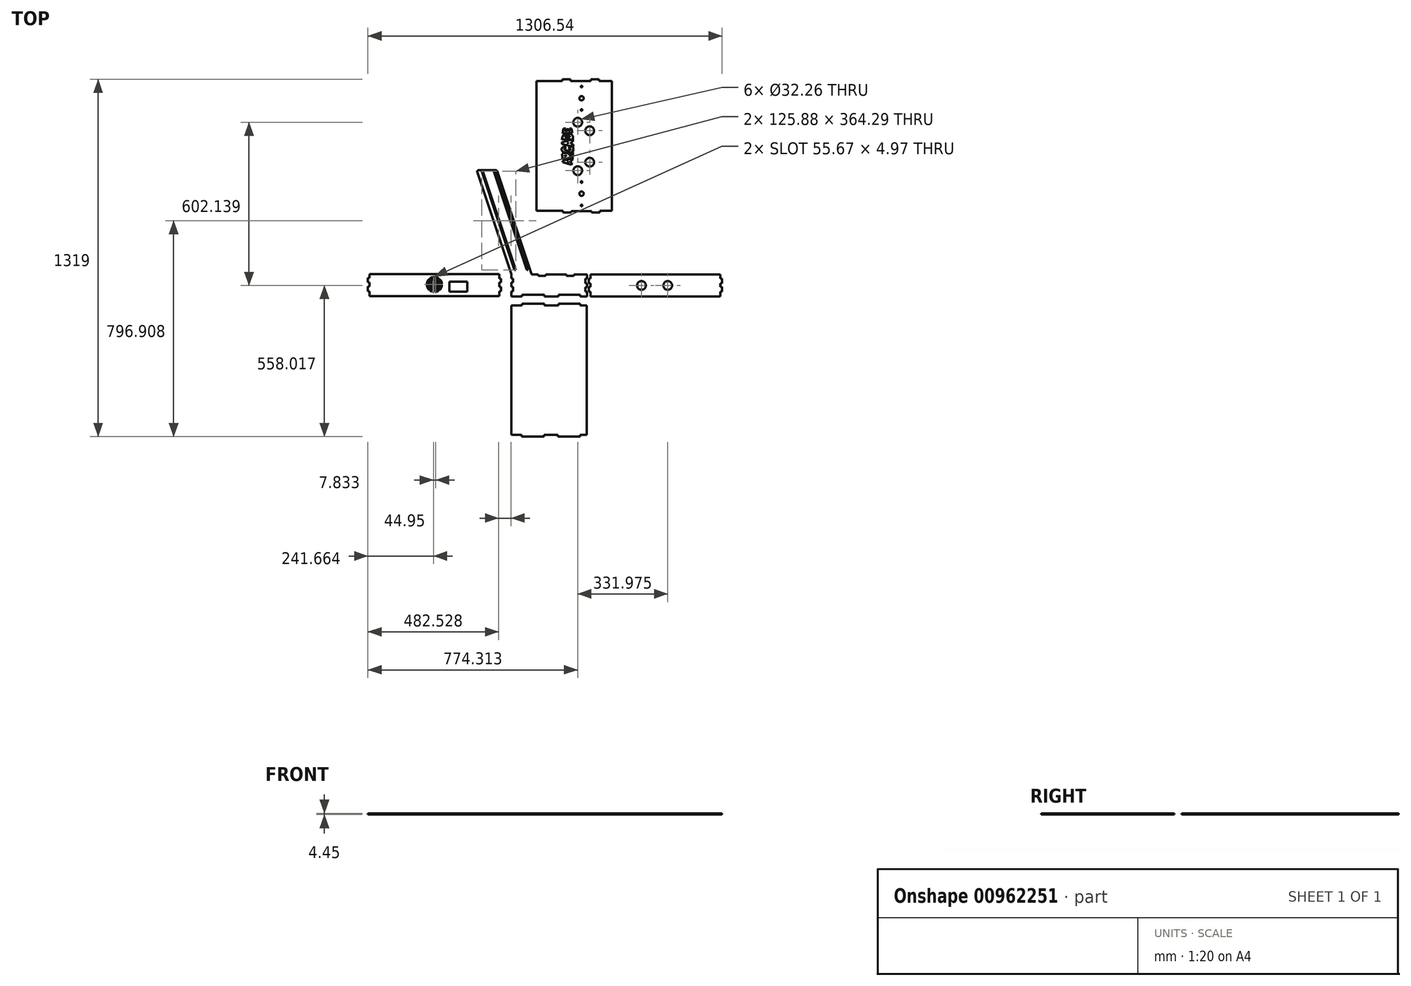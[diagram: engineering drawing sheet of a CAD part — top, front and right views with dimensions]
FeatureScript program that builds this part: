
annotation { "Feature Type Name" : "Feature", "Feature Type Description" : "" }
export const myFeature = defineFeature(function(context is Context, id is Id, definition is map)
    precondition{}
    {
        {
            var Q0;
            Q0=qCreatedBy(makeId("Top.planeOp"),FACE);
            var sketch = newSketch(context, id + "F0", { "sketchPlane" : qUnion([Q0])});
            skLineSegment(sketch, "E0.0", {"start": v(-133.22, 195.57) * mm, "end": v(-13.13, -164.7) * mm});
            skLineSegment(sketch, "E0.2", {"start": v(-206.4, 192.41) * mm, "end": v(-84, -174.81) * mm});
            skLineSegment(sketch, "E1", {"start": v(-84, -174.81) * mm, "end": v(-80.85, -184.23) * mm});
            skLineSegment(sketch, "E2", {"start": v(-13.13, -164.7) * mm, "end": v(-7.25, -182.33) * mm});
            skPoint(sketch, "E3.start.orphan", {"position": v(-23.94, -169.52) * mm});
            skLineSegment(sketch, "E4.bottom", {"start": v(-2.51, -185.75) * mm, "end": v(17.92, -185.75) * mm});
            skLineSegment(sketch, "E4.right", {"start": v(199.34, -185.75) * mm, "end": v(199.34, -201.04) * mm});
            skLineSegment(sketch, "E5", {"start": v(-129.53, 12.4) * mm, "end": v(-125.08, 12.4) * mm});
            skLineSegment(sketch, "E6", {"start": v(-89.03, 12.4) * mm, "end": v(-93.48, 12.4) * mm});
            skLineSegment(sketch, "E7.left", {"start": v(-80.35, -185.75) * mm, "end": v(-80.35, -201.04) * mm});
            skPoint(sketch, "E8.end.orphan", {"position": v(-48.56, -185.75) * mm});
            skLineSegment(sketch, "E9", {"start": v(-188.02, 199) * mm, "end": v(-201.66, 199) * mm});
            skLineSegment(sketch, "E10", {"start": v(-188.02, 199) * mm, "end": v(-137.97, 199) * mm});
            skPoint(sketch, "E11.start.orphan", {"position": v(-188.02, 194.54) * mm});
            skLineSegment(sketch, "E12.bottom", {"start": v(45.83, -190.2) * mm, "end": v(18.43, -190.2) * mm});
            skLineSegment(sketch, "E12.left", {"start": v(45.83, -190.2) * mm, "end": v(45.32, -185.75) * mm});
            skLineSegment(sketch, "E12.right", {"start": v(18.43, -190.2) * mm, "end": v(17.92, -185.75) * mm});
            skPoint(sketch, "E12.middle", {"position": v(31.62, -185.75) * mm});
            skPoint(sketch, "E13.middle", {"position": v(159.6, -185.75) * mm});
            skPoint(sketch, "E12.top.end.orphan", {"position": v(17.41, -181.3) * mm});
            skPoint(sketch, "E14.orphan", {"position": v(44.81, -181.3) * mm});
            skPoint(sketch, "E13.top.end.orphan", {"position": v(142.34, -174.18) * mm});
            skPoint(sketch, "E15.orphan", {"position": v(176.85, -174.18) * mm});
            skLineSegment(sketch, "E16.bottom", {"start": v(149.99, -190.2) * mm, "end": v(122.59, -190.2) * mm});
            skLineSegment(sketch, "E16.left", {"start": v(149.99, -190.2) * mm, "end": v(149.98, -185.75) * mm});
            skLineSegment(sketch, "E16.right", {"start": v(122.59, -190.2) * mm, "end": v(122.58, -185.75) * mm});
            skLineSegment(sketch, "E17.trimOffspring", {"start": v(45.32, -185.75) * mm, "end": v(122.58, -185.75) * mm});
            skLineSegment(sketch, "E18.trimOffspring", {"start": v(149.98, -185.75) * mm, "end": v(199.34, -185.75) * mm});
            skLineSegment(sketch, "E19.bottom", {"start": v(199.34, -218.57) * mm, "end": v(193, -218.57) * mm});
            skLineSegment(sketch, "E19.top", {"start": v(199.34, -201.04) * mm, "end": v(193, -201.04) * mm});
            skLineSegment(sketch, "E19.right", {"start": v(193, -218.57) * mm, "end": v(193, -201.04) * mm});
            skPoint(sketch, "E19.middle", {"position": v(199.34, -209.8) * mm});
            skPoint(sketch, "E19.left.end.orphan", {"position": v(205.67, -201.04) * mm});
            skPoint(sketch, "E20.orphan", {"position": v(205.67, -218.57) * mm});
            skLineSegment(sketch, "E21.trimOffspring", {"start": v(199.34, -218.57) * mm, "end": v(199.34, -232.97) * mm});
            skLineSegment(sketch, "E22.bottom", {"start": v(199.34, -248.5) * mm, "end": v(193, -248.5) * mm});
            skLineSegment(sketch, "E22.top", {"start": v(199.34, -232.97) * mm, "end": v(193, -232.97) * mm});
            skLineSegment(sketch, "E22.right", {"start": v(193, -248.5) * mm, "end": v(193, -232.97) * mm});
            skLineSegment(sketch, "E23.trimOffspring", {"start": v(199.34, -248.5) * mm, "end": v(199.34, -266.77) * mm});
            skLineSegment(sketch, "E24.bottom", {"start": v(109.66, 43.6) * mm, "end": v(140.06, 43.6) * mm});
            skLineSegment(sketch, "E24.left", {"start": v(109.66, 43.6) * mm, "end": v(109.66, 49.94) * mm});
            skLineSegment(sketch, "E24.right", {"start": v(140.06, 43.6) * mm, "end": v(140.06, 48.06) * mm});
            skLineSegment(sketch, "E25.top", {"start": v(214.83, 43.6) * mm, "end": v(245.23, 43.6) * mm});
            skLineSegment(sketch, "E25.left", {"start": v(214.83, 48.06) * mm, "end": v(214.83, 43.6) * mm});
            skLineSegment(sketch, "E25.right", {"start": v(245.23, 49.94) * mm, "end": v(245.23, 43.6) * mm});
            skLineSegment(sketch, "E26", {"start": v(86.13, 49.94) * mm, "end": v(109.66, 49.94) * mm});
            skLineSegment(sketch, "E27", {"start": v(140.06, 48.06) * mm, "end": v(214.83, 48.06) * mm});
            skLineSegment(sketch, "E28", {"start": v(245.23, 49.94) * mm, "end": v(289.7, 49.94) * mm});
            skLineSegment(sketch, "E29", {"start": v(289.7, 49.94) * mm, "end": v(289.7, 528.39) * mm});
            skLineSegment(sketch, "E30", {"start": v(86.13, 528.39) * mm, "end": v(107.66, 528.39) * mm});
            skLineSegment(sketch, "E31.MirrorCS", {"start": v(107.66, 534.72) * mm, "end": v(107.66, 528.39) * mm});
            skLineSegment(sketch, "E32.MirrorCS", {"start": v(138.06, 534.72) * mm, "end": v(138.06, 528.39) * mm});
            skLineSegment(sketch, "E33.MirrorCS", {"start": v(212.83, 528.39) * mm, "end": v(212.83, 534.72) * mm});
            skLineSegment(sketch, "E34.MirrorCS", {"start": v(243.23, 528.39) * mm, "end": v(243.23, 534.72) * mm});
            skLineSegment(sketch, "E35.trimOffspring", {"start": v(138.06, 528.39) * mm, "end": v(212.83, 528.39) * mm});
            skLineSegment(sketch, "E36.trimOffspring", {"start": v(243.23, 528.39) * mm, "end": v(289.7, 528.39) * mm});
            skPoint(sketch, "E37.start.orphan", {"position": v(86.13, 289.16) * mm});
            skCircle(sketch, "E38", {"center": v(178.38, 507.69) * mm, "radius": 3 * mm});
            skCircle(sketch, "E39", {"center": v(178.38, 421.29) * mm, "radius": 3 * mm});
            skCircle(sketch, "E40", {"center": v(164.4, 375.88) * mm, "radius": 16.13 * mm});
            skCircle(sketch, "E41", {"center": v(208.47, 344.63) * mm, "radius": 16.13 * mm});
            skCircle(sketch, "E42.MirrorC", {"center": v(178.38, 155.57) * mm, "radius": 3 * mm});
            skCircle(sketch, "E43.MirrorC", {"center": v(178.38, 69.17) * mm, "radius": 3 * mm});
            skCircle(sketch, "E44.MirrorC", {"center": v(208.47, 228.58) * mm, "radius": 16.13 * mm});
            skCircle(sketch, "E45.MirrorC", {"center": v(164.4, 197.33) * mm, "radius": 16.13 * mm});
            skCircle(sketch, "E46", {"center": v(178.38, 464.49) * mm, "radius": 8.09 * mm});
            skCircle(sketch, "E47.MirrorC", {"center": v(178.38, 112.37) * mm, "radius": 8.09 * mm});
            skLineSegment(sketch, "E48.MirrorCS", {"start": v(120.12, 254.5) * mm, "end": v(118.38, 254.37) * mm});
            skLineSegment(sketch, "E49.MirrorCS", {"start": v(146.92, 313.16) * mm, "end": v(146.92, 304.04) * mm});
            skLineSegment(sketch, "E50.MirrorCS", {"start": v(146.24, 313.22) * mm, "end": v(146.92, 313.16) * mm});
            skLineSegment(sketch, "E51.MirrorCS", {"start": v(117.25, 254.08) * mm, "end": v(116.34, 253.4) * mm});
            skLineSegment(sketch, "E52.MirrorCS", {"start": v(116.34, 253.4) * mm, "end": v(116, 250.63) * mm});
            skLineSegment(sketch, "E53.MirrorCS", {"start": v(129.87, 228.95) * mm, "end": v(129.87, 231.1) * mm});
            skLineSegment(sketch, "E54.MirrorCS", {"start": v(118.38, 254.37) * mm, "end": v(117.25, 254.08) * mm});
            skLineSegment(sketch, "E55.MirrorCS", {"start": v(121.7, 253.4) * mm, "end": v(120.12, 254.5) * mm});
            skLineSegment(sketch, "E56.MirrorCS", {"start": v(142.11, 234.25) * mm, "end": v(144.38, 234.25) * mm});
            skLineSegment(sketch, "E57.MirrorCS", {"start": v(123.2, 262.9) * mm, "end": v(122.67, 262.98) * mm});
            skLineSegment(sketch, "E58.MirrorCS", {"start": v(116, 250.63) * mm, "end": v(121.7, 250.43) * mm});
            skLineSegment(sketch, "E59.MirrorCS", {"start": v(144.64, 304.04) * mm, "end": v(140.36, 303.04) * mm});
            skLineSegment(sketch, "E60.MirrorCS", {"start": v(121.7, 250.43) * mm, "end": v(121.7, 253.4) * mm});
            skLineSegment(sketch, "E61.MirrorCS", {"start": v(130.78, 258.7) * mm, "end": v(128.56, 260.6) * mm});
            skLineSegment(sketch, "E62.MirrorCS", {"start": v(145.83, 241.97) * mm, "end": v(144.38, 234.25) * mm});
            skLineSegment(sketch, "E63.MirrorCS", {"start": v(138.33, 233.06) * mm, "end": v(142.11, 234.25) * mm});
            skLineSegment(sketch, "E64.MirrorCS", {"start": v(145.08, 255.03) * mm, "end": v(146.64, 255.34) * mm});
            skLineSegment(sketch, "E65.MirrorCS", {"start": v(142.65, 241.97) * mm, "end": v(145.83, 241.97) * mm});
            skLineSegment(sketch, "E66.MirrorCS", {"start": v(140.36, 296.24) * mm, "end": v(145.28, 294.98) * mm});
            skLineSegment(sketch, "E67.MirrorCS", {"start": v(146.92, 304.04) * mm, "end": v(144.64, 304.04) * mm});
            skLineSegment(sketch, "E68.MirrorCS", {"start": v(145.9, 250.5) * mm, "end": v(132.72, 250.5) * mm});
            skLineSegment(sketch, "E69.MirrorCS", {"start": v(140.36, 303.04) * mm, "end": v(140.36, 296.24) * mm});
            skLineSegment(sketch, "E70.MirrorCS", {"start": v(125.05, 299.5) * mm, "end": v(130.81, 298.2) * mm});
            skLineSegment(sketch, "E71.MirrorCS", {"start": v(129.87, 231.1) * mm, "end": v(125.64, 230.28) * mm});
            skLineSegment(sketch, "E72.MirrorCS", {"start": v(123, 224.26) * mm, "end": v(134.99, 220.38) * mm});
            skLineSegment(sketch, "E73.MirrorCS", {"start": v(145.28, 294.98) * mm, "end": v(147.53, 294.98) * mm});
            skLineSegment(sketch, "E74.MirrorCS", {"start": v(130.81, 298.2) * mm, "end": v(130.81, 300.81) * mm});
            skLineSegment(sketch, "E75.MirrorCS", {"start": v(145.62, 242.56) * mm, "end": v(145.9, 250.5) * mm});
            skLineSegment(sketch, "E76.MirrorCS", {"start": v(125.64, 230.28) * mm, "end": v(129.87, 228.95) * mm});
            skLineSegment(sketch, "E77.MirrorCS", {"start": v(141.03, 226.32) * mm, "end": v(137.8, 226.9) * mm});
            skLineSegment(sketch, "E78.MirrorCS", {"start": v(137.8, 226.9) * mm, "end": v(138.33, 233.06) * mm});
            skLineSegment(sketch, "E79.MirrorCS", {"start": v(132.72, 250.5) * mm, "end": v(145.08, 255.03) * mm});
            skLineSegment(sketch, "E80.MirrorCS", {"start": v(147.3, 264.53) * mm, "end": v(130.78, 258.7) * mm});
            skLineSegment(sketch, "E81.MirrorCS", {"start": v(146.64, 255.34) * mm, "end": v(147.3, 264.53) * mm});
            skLineSegment(sketch, "E82.MirrorCS", {"start": v(130.81, 300.81) * mm, "end": v(125.05, 299.5) * mm});
            skLineSegment(sketch, "E83.MirrorCS", {"start": v(143.46, 226.32) * mm, "end": v(141.03, 226.32) * mm});
            skLineSegment(sketch, "E84.MirrorCS", {"start": v(142.65, 241.97) * mm, "end": v(128.56, 238.4) * mm});
            skLineSegment(sketch, "E85.MirrorCS", {"start": v(140.12, 218.92) * mm, "end": v(141.84, 218.2) * mm});
            skLineSegment(sketch, "E86.MirrorCS", {"start": v(135.95, 321.28) * mm, "end": v(135.67, 323.92) * mm});
            skArc(sketch, "E87.MirrorCS", {"start": v(135.67, 323.92) * mm, "mid": v(126.36, 327.54) * mm, "end": v(117.25, 323.41) * mm});
            skLineSegment(sketch, "E88.MirrorCS", {"start": v(107.46, 243.91) * mm, "end": v(145.62, 242.56) * mm});
            skLineSegment(sketch, "E89.MirrorCS", {"start": v(141.84, 218.2) * mm, "end": v(143.46, 226.32) * mm});
            skFitSpline(sketch, "E90.MirrorCS", {"points": [v(128.56, 260.6) * mm, v(123.2, 262.9) * mm, v(114.65, 262.9) * mm, v(107.11, 257.92) * mm, v(107.34, 246.66) * mm, v(107.46, 243.91) * mm, v(131.36, 256.58) * mm, v(128.56, 260.6) * mm]});
            skLineSegment(sketch, "E91.MirrorCS", {"start": v(117.25, 321.28) * mm, "end": v(135.95, 321.28) * mm});
            skLineSegment(sketch, "E92.MirrorCS", {"start": v(131.27, 342.19) * mm, "end": v(130.03, 350.78) * mm});
            skArc(sketch, "E93.MirrorCS", {"start": v(146.24, 324.8) * mm, "mid": v(125.43, 335.33) * mm, "end": v(107.15, 320.84) * mm});
            skLineSegment(sketch, "E94.MirrorCS", {"start": v(108.97, 235.06) * mm, "end": v(109.67, 228.58) * mm});
            skLineSegment(sketch, "E95.MirrorCS", {"start": v(117.25, 341.92) * mm, "end": v(119.47, 353.18) * mm});
            skLineSegment(sketch, "E96.MirrorCS", {"start": v(122.84, 350.78) * mm, "end": v(122.84, 341.92) * mm});
            skLineSegment(sketch, "E97.MirrorCS", {"start": v(134.15, 353.36) * mm, "end": v(135.67, 342.82) * mm});
            skLineSegment(sketch, "E98.MirrorCS", {"start": v(109.67, 228.58) * mm, "end": v(123, 224.26) * mm});
            skLineSegment(sketch, "E99.MirrorCS", {"start": v(119.47, 353.18) * mm, "end": v(111.45, 352.62) * mm});
            skLineSegment(sketch, "E100.MirrorCS", {"start": v(135.67, 342.82) * mm, "end": v(131.27, 342.19) * mm});
            skLineSegment(sketch, "E101.MirrorCS", {"start": v(117.25, 323.41) * mm, "end": v(117.25, 321.28) * mm});
            skLineSegment(sketch, "E102.MirrorCS", {"start": v(147.5, 285.67) * mm, "end": v(105.6, 295.49) * mm});
            skLineSegment(sketch, "E103.MirrorCS", {"start": v(141.7, 353.36) * mm, "end": v(134.15, 353.36) * mm});
            skLineSegment(sketch, "E104.MirrorCS", {"start": v(105.6, 295.49) * mm, "end": v(105.6, 302.4) * mm});
            skLineSegment(sketch, "E105.MirrorCS", {"start": v(130.03, 350.78) * mm, "end": v(122.84, 350.78) * mm});
            skLineSegment(sketch, "E106.MirrorCS", {"start": v(128.56, 238.4) * mm, "end": v(108.97, 235.06) * mm});
            skLineSegment(sketch, "E107.MirrorCS", {"start": v(122.84, 341.92) * mm, "end": v(117.25, 341.92) * mm});
            skLineSegment(sketch, "E108.MirrorCS", {"start": v(111.45, 352.62) * mm, "end": v(108.28, 334.85) * mm});
            skLineSegment(sketch, "E109.MirrorCS", {"start": v(134.99, 220.38) * mm, "end": v(140.12, 218.92) * mm});
            skLineSegment(sketch, "E110.MirrorCS", {"start": v(146.92, 313.7) * mm, "end": v(146.24, 324.8) * mm});
            skLineSegment(sketch, "E111.MirrorCS", {"start": v(105.6, 302.4) * mm, "end": v(146.24, 313.22) * mm});
            skLineSegment(sketch, "E112.MirrorCS", {"start": v(106.5, 312.6) * mm, "end": v(146.92, 313.7) * mm});
            skLineSegment(sketch, "E113.MirrorCS", {"start": v(106.5, 312.6) * mm, "end": v(107.15, 320.84) * mm});
            skLineSegment(sketch, "E114.MirrorCS", {"start": v(143.98, 337.2) * mm, "end": v(141.7, 353.36) * mm});
            skLineSegment(sketch, "E115.MirrorCS", {"start": v(108.28, 334.85) * mm, "end": v(143.98, 337.2) * mm});
            skFitSpline(sketch, "E116.MirrorC", {"points": [v(118.4, 278.2) * mm, v(116.6, 278.05) * mm, v(114.9, 277.2) * mm, v(114.56, 275.62) * mm, v(115.92, 274) * mm, v(121.92, 272.13) * mm, v(128.49, 271.77) * mm, v(134.71, 272.58) * mm, v(138, 274.5) * mm, v(138.34, 276.84) * mm, v(135.73, 277.9) * mm, v(132.68, 278.86) * mm, v(132.68, 279.68) * mm, v(132.62, 286.61) * mm, v(132.68, 287.83) * mm, v(142.87, 285.6) * mm, v(143.54, 285.19) * mm, v(147.96, 281.4) * mm, v(148.3, 273.3) * mm, v(145.36, 268.33) * mm, v(137.77, 264.48) * mm, v(126.67, 263.32) * mm, v(115.01, 264.89) * mm, v(108.45, 268.48) * mm, v(105.05, 272.38) * mm, v(104.54, 276.89) * mm, v(106.18, 281.85) * mm, v(112.01, 286) * mm, v(117.28, 287.53) * mm, v(118.4, 287.58) * mm, v(118.64, 285.19) * mm, v(118.4, 278.2) * mm]});
            skLineSegment(sketch, "E117", {"start": v(147.53, 294.98) * mm, "end": v(147.5, 285.67) * mm});
            skLineSegment(sketch, "E118.bottom", {"start": v(211.85, -185.75) * mm, "end": v(690.3, -185.75) * mm});
            skLineSegment(sketch, "E118.top", {"start": v(211.85, -266.77) * mm, "end": v(690.3, -266.77) * mm});
            skLineSegment(sketch, "E118.left", {"start": v(211.85, -185.75) * mm, "end": v(211.85, -201.04) * mm});
            skLineSegment(sketch, "E118.right", {"start": v(690.3, -185.75) * mm, "end": v(690.3, -201.04) * mm});
            skLineSegment(sketch, "E119.bottom", {"start": v(211.85, -201.04) * mm, "end": v(205.52, -201.04) * mm});
            skLineSegment(sketch, "E119.top", {"start": v(211.85, -218.57) * mm, "end": v(205.52, -218.57) * mm});
            skLineSegment(sketch, "E119.right", {"start": v(205.52, -201.04) * mm, "end": v(205.52, -218.57) * mm});
            skLineSegment(sketch, "E120.top", {"start": v(211.85, -248.5) * mm, "end": v(205.52, -248.5) * mm});
            skLineSegment(sketch, "E120.right", {"start": v(205.52, -230.97) * mm, "end": v(205.52, -248.5) * mm});
            skCircle(sketch, "E121", {"center": v(399.43, -226.26) * mm, "radius": 16.13 * mm});
            skPoint(sketch, "E121.centerSnap0", {"position": v(211.85, -226.26) * mm});
            skCircle(sketch, "E122.MirrorC", {"center": v(496.38, -226.26) * mm, "radius": 16.13 * mm});
            skPoint(sketch, "E123.start.orphan", {"position": v(451.07, -185.75) * mm});
            skLineSegment(sketch, "E124.MirrorCS", {"start": v(690.3, -230.97) * mm, "end": v(696.63, -230.97) * mm});
            skLineSegment(sketch, "E125.MirrorCS", {"start": v(690.3, -248.5) * mm, "end": v(696.63, -248.5) * mm});
            skLineSegment(sketch, "E126.MirrorCS", {"start": v(690.3, -218.57) * mm, "end": v(696.63, -218.57) * mm});
            skLineSegment(sketch, "E127.MirrorCS", {"start": v(690.3, -201.04) * mm, "end": v(696.63, -201.04) * mm});
            skLineSegment(sketch, "E128.trimOffspring", {"start": v(211.85, -218.57) * mm, "end": v(211.85, -226.26) * mm});
            skLineSegment(sketch, "E129.trimOffspring", {"start": v(211.85, -248.5) * mm, "end": v(211.85, -266.77) * mm});
            skLineSegment(sketch, "E130.trimOffspring", {"start": v(690.3, -248.5) * mm, "end": v(690.3, -266.77) * mm});
            skLineSegment(sketch, "E131.trimOffspring", {"start": v(690.3, -218.57) * mm, "end": v(690.3, -230.97) * mm});
            skLineSegment(sketch, "E132.trimOffspring", {"start": v(-80.35, -248.5) * mm, "end": v(-80.35, -266.77) * mm});
            skPoint(sketch, "E133.start.orphan", {"position": v(59.5, -266.77) * mm});
            skPoint(sketch, "E134.middle", {"position": v(-577.81, -208.7) * mm});
            skPoint(sketch, "E134.left.end.orphan", {"position": v(-573.36, -199.94) * mm});
            skPoint(sketch, "E135.orphan", {"position": v(-573.36, -217.46) * mm});
            skLineSegment(sketch, "E136.bottom", {"start": v(-603.58, -184.65) * mm, "end": v(-125.08, -184.65) * mm});
            skLineSegment(sketch, "E136.top", {"start": v(-603.58, -265.67) * mm, "end": v(-125.08, -265.67) * mm});
            skLineSegment(sketch, "E136.left", {"start": v(-603.58, -184.65) * mm, "end": v(-603.58, -197.94) * mm});
            skLineSegment(sketch, "E136.right", {"start": v(-125.08, -184.65) * mm, "end": v(-125.08, -200.94) * mm});
            skLineSegment(sketch, "E137.bottom", {"start": v(-603.58, -197.94) * mm, "end": v(-609.9, -197.94) * mm});
            skLineSegment(sketch, "E137.top", {"start": v(-603.58, -215.46) * mm, "end": v(-609.9, -215.46) * mm});
            skLineSegment(sketch, "E137.right", {"start": v(-609.9, -197.94) * mm, "end": v(-609.9, -215.46) * mm});
            skLineSegment(sketch, "E138.bottom", {"start": v(-603.58, -229.86) * mm, "end": v(-609.9, -229.86) * mm});
            skLineSegment(sketch, "E138.top", {"start": v(-603.58, -247.39) * mm, "end": v(-609.9, -247.39) * mm});
            skLineSegment(sketch, "E138.right", {"start": v(-609.9, -229.86) * mm, "end": v(-609.9, -247.39) * mm});
            skPoint(sketch, "E139.centerSnap0", {"position": v(-563.42, -225.16) * mm});
            skPoint(sketch, "E140.start.orphan", {"position": v(-324.17, -184.65) * mm});
            skLineSegment(sketch, "E141.MirrorCS", {"start": v(-125.08, -247.39) * mm, "end": v(-118.75, -247.39) * mm});
            skLineSegment(sketch, "E142.MirrorCS", {"start": v(-125.08, -215.46) * mm, "end": v(-118.75, -215.46) * mm});
            skLineSegment(sketch, "E143.MirrorCS", {"start": v(-125.08, -200.94) * mm, "end": v(-118.75, -200.94) * mm});
            skLineSegment(sketch, "E144.trimOffspring", {"start": v(-603.58, -215.46) * mm, "end": v(-603.58, -229.86) * mm});
            skLineSegment(sketch, "E145.trimOffspring", {"start": v(-603.58, -247.39) * mm, "end": v(-603.58, -265.67) * mm});
            skLineSegment(sketch, "E146.trimOffspring", {"start": v(-125.08, -247.39) * mm, "end": v(-125.08, -265.67) * mm});
            skLineSegment(sketch, "E147.trimOffspring", {"start": v(-125.08, -215.46) * mm, "end": v(-125.08, -229.86) * mm});
            skPoint(sketch, "E148.middle", {"position": v(0, -266.77) * mm});
            skPoint(sketch, "E149.orphan", {"position": v(-41.14, -273.1) * mm});
            skPoint(sketch, "E150.orphan", {"position": v(41.14, -273.1) * mm});
            skLineSegment(sketch, "E151.bottom", {"start": v(-80.35, -299.5) * mm, "end": v(-41.14, -299.5) * mm});
            skLineSegment(sketch, "E151.left", {"start": v(-80.35, -299.5) * mm, "end": v(-80.35, -773.5) * mm});
            skLineSegment(sketch, "E152.top", {"start": v(93.97, -293.17) * mm, "end": v(172.76, -293.17) * mm});
            skLineSegment(sketch, "E152.left", {"start": v(93.97, -299.5) * mm, "end": v(93.97, -293.17) * mm});
            skLineSegment(sketch, "E153.trimOffspring", {"start": v(41.14, -299.5) * mm, "end": v(93.97, -299.5) * mm});
            skLineSegment(sketch, "E154.trimOffspring", {"start": v(175.66, -299.5) * mm, "end": v(197.46, -299.5) * mm});
            skLineSegment(sketch, "E155.MirrorCS", {"start": v(-42.14, -773.5) * mm, "end": v(-42.14, -777.95) * mm});
            skLineSegment(sketch, "E156.MirrorCS", {"start": v(40.14, -777.95) * mm, "end": v(40.14, -784.28) * mm});
            skLineSegment(sketch, "E157.MirrorCS", {"start": v(91.37, -777.95) * mm, "end": v(91.37, -784.28) * mm});
            skLineSegment(sketch, "E158.MirrorCS", {"start": v(173.66, -777.95) * mm, "end": v(173.66, -784.28) * mm});
            skLineSegment(sketch, "E159.trimOffspring", {"start": v(40.14, -777.95) * mm, "end": v(91.37, -777.95) * mm});
            skPoint(sketch, "E160.start.orphan", {"position": v(-80.35, -536.5) * mm});
            skLineSegment(sketch, "E161.trimOffspring", {"start": v(173.66, -777.95) * mm, "end": v(197.46, -777.95) * mm});
            skLineSegment(sketch, "E162", {"start": v(696.63, -201.04) * mm, "end": v(696.63, -218.57) * mm});
            skLineSegment(sketch, "E163", {"start": v(696.63, -230.97) * mm, "end": v(696.63, -248.5) * mm});
            skLineSegment(sketch, "E164", {"start": v(-118.75, -215.46) * mm, "end": v(-118.75, -200.94) * mm});
            skLineSegment(sketch, "E165", {"start": v(-118.75, -230.86) * mm, "end": v(-118.75, -247.39) * mm});
            skLineSegment(sketch, "E166", {"start": v(107.66, 534.72) * mm, "end": v(138.06, 534.72) * mm});
            skLineSegment(sketch, "E167", {"start": v(212.83, 534.72) * mm, "end": v(243.23, 534.72) * mm});
            skLineSegment(sketch, "E168", {"start": v(173.66, -784.28) * mm, "end": v(91.37, -784.28) * mm});
            skLineSegment(sketch, "E169", {"start": v(40.14, -784.28) * mm, "end": v(-42.14, -784.28) * mm});
            skLineSegment(sketch, "E170", {"start": v(-42.14, -784.28) * mm, "end": v(-42.14, -777.95) * mm});
            skLineSegment(sketch, "E171", {"start": v(-80.35, -773.5) * mm, "end": v(-80.35, -777.95) * mm});
            skLineSegment(sketch, "E172", {"start": v(-80.35, -777.95) * mm, "end": v(-42.14, -777.95) * mm});
            skLineSegment(sketch, "E173.bottom", {"start": v(86.13, 49.94) * mm, "end": v(11.9, 49.94) * mm});
            skLineSegment(sketch, "E173.top", {"start": v(86.13, 528.39) * mm, "end": v(11.9, 528.39) * mm});
            skLineSegment(sketch, "E173.right", {"start": v(11.9, 49.94) * mm, "end": v(11.9, 528.39) * mm});
            skLineSegment(sketch, "E174", {"start": v(-190.32, 194.78) * mm, "end": v(-68.9, -169.52) * mm});
            skLineSegment(sketch, "E175", {"start": v(-64.44, -169.52) * mm, "end": v(-68.9, -169.52) * mm});
            skLineSegment(sketch, "E176", {"start": v(-125.16, 12.63) * mm, "end": v(-185.87, 194.78) * mm});
            skLineSegment(sketch, "E177", {"start": v(-125.16, 12.63) * mm, "end": v(-64.44, -169.52) * mm});
            skLineSegment(sketch, "E178.trimOffspring", {"start": v(-185.87, 194.78) * mm, "end": v(-190.32, 194.78) * mm});
            skLineSegment(sketch, "E179", {"start": v(-140.92, 194.78) * mm, "end": v(-19.5, -169.52) * mm});
            skLineSegment(sketch, "E180", {"start": v(-140.92, 194.78) * mm, "end": v(-145.37, 194.78) * mm});
            skLineSegment(sketch, "E181", {"start": v(-23.94, -169.52) * mm, "end": v(-19.5, -169.52) * mm});
            skLineSegment(sketch, "E182", {"start": v(-84.66, 12.63) * mm, "end": v(-23.94, -169.52) * mm});
            skLineSegment(sketch, "E183", {"start": v(-84.66, 12.63) * mm, "end": v(-145.37, 194.78) * mm});
            skLineSegment(sketch, "E184.top", {"start": v(-41.14, -293.17) * mm, "end": v(41.14, -293.17) * mm});
            skLineSegment(sketch, "E184.left", {"start": v(-41.14, -299.5) * mm, "end": v(-41.14, -293.17) * mm});
            skLineSegment(sketch, "E184.right", {"start": v(41.14, -299.5) * mm, "end": v(41.14, -293.17) * mm});
            skLineSegment(sketch, "E185.MirrorCS", {"start": v(172.76, -293.17) * mm, "end": v(93.97, -293.17) * mm});
            skPoint(sketch, "E186.start.orphan", {"position": v(67.56, -299.5) * mm});
            skPoint(sketch, "E187.orphan", {"position": v(211.85, -232.97) * mm});
            skLineSegment(sketch, "E188", {"start": v(211.85, -218.57) * mm, "end": v(211.85, -230.97) * mm});
            skLineSegment(sketch, "E189", {"start": v(211.85, -230.97) * mm, "end": v(205.52, -230.97) * mm});
            skArc(sketch, "E190", {"start": v(-357.93, -195.54) * mm, "mid": v(-360.4, -195.07) * mm, "end": v(-362.9, -194.83) * mm});
            skPoint(sketch, "E190.centerSnap0", {"position": v(-125.08, -222.66) * mm});
            skPoint(sketch, "E190.centerSnap1", {"position": v(-364.33, -184.65) * mm});
            skLineSegment(sketch, "E191.left", {"start": v(-362.9, -250.5) * mm, "end": v(-362.9, -194.83) * mm});
            skLineSegment(sketch, "E191.right", {"start": v(-365.76, -250.5) * mm, "end": v(-365.76, -194.83) * mm});
            skLineSegment(sketch, "E192.left", {"start": v(-355.09, -248.96) * mm, "end": v(-355.09, -196.37) * mm});
            skLineSegment(sketch, "E192.right", {"start": v(-357.93, -249.79) * mm, "end": v(-357.93, -195.54) * mm});
            skPoint(sketch, "E192.middle", {"position": v(-356.5, -222.66) * mm});
            skPoint(sketch, "E192.middle.positionSnap0", {"position": v(-362.9, -222.66) * mm});
            skPoint(sketch, "E192.centerSnap0", {"position": v(-362.9, -222.66) * mm});
            skLineSegment(sketch, "E193.left", {"start": v(-348.17, -245.37) * mm, "end": v(-348.17, -199.96) * mm});
            skLineSegment(sketch, "E193.right", {"start": v(-345.33, -243.05) * mm, "end": v(-345.33, -202.28) * mm});
            skPoint(sketch, "E193.middle", {"position": v(-346.75, -222.66) * mm});
            skLineSegment(sketch, "E194.MirrorCS", {"start": v(-370.73, -249.79) * mm, "end": v(-370.73, -195.54) * mm});
            skLineSegment(sketch, "E195.MirrorCS", {"start": v(-373.57, -248.96) * mm, "end": v(-373.57, -196.37) * mm});
            skLineSegment(sketch, "E196.MirrorCS", {"start": v(-380.5, -245.37) * mm, "end": v(-380.5, -199.96) * mm});
            skLineSegment(sketch, "E197.MirrorCS", {"start": v(-383.33, -243.05) * mm, "end": v(-383.33, -202.28) * mm});
            skPoint(sketch, "E191.top.end.orphan", {"position": v(-365.76, -190.84) * mm});
            skPoint(sketch, "E191.top.start.orphan", {"position": v(-362.9, -190.84) * mm});
            skPoint(sketch, "E198.orphan", {"position": v(-370.73, -189.78) * mm});
            skPoint(sketch, "E199.orphan", {"position": v(-373.57, -189.78) * mm});
            skPoint(sketch, "E200.orphan", {"position": v(-383.33, -192.62) * mm});
            skPoint(sketch, "E201.orphan", {"position": v(-380.5, -192.62) * mm});
            skPoint(sketch, "E192.top.end.orphan", {"position": v(-357.93, -189.78) * mm});
            skPoint(sketch, "E192.top.start.orphan", {"position": v(-355.09, -189.78) * mm});
            skPoint(sketch, "E193.top.end.orphan", {"position": v(-345.33, -192.62) * mm});
            skPoint(sketch, "E193.top.start.orphan", {"position": v(-348.17, -192.62) * mm});
            skArc(sketch, "E202.trimOffspring", {"start": v(-365.76, -194.83) * mm, "mid": v(-368.26, -195.07) * mm, "end": v(-370.73, -195.54) * mm});
            skArc(sketch, "E203.trimOffspring", {"start": v(-383.33, -202.28) * mm, "mid": v(-392.2, -222.66) * mm, "end": v(-383.33, -243.05) * mm});
            skArc(sketch, "E204.trimOffspring", {"start": v(-370.73, -249.79) * mm, "mid": v(-368.26, -250.25) * mm, "end": v(-365.76, -250.5) * mm});
            skArc(sketch, "E205.trimOffspring", {"start": v(-362.9, -250.5) * mm, "mid": v(-360.4, -250.25) * mm, "end": v(-357.93, -249.79) * mm});
            skArc(sketch, "E206.trimOffspring", {"start": v(-355.09, -248.96) * mm, "mid": v(-351.5, -247.4) * mm, "end": v(-348.17, -245.37) * mm});
            skArc(sketch, "E207.trimOffspring", {"start": v(-345.33, -243.05) * mm, "mid": v(-337.05, -216.96) * mm, "end": v(-355.09, -196.37) * mm});
            skPoint(sketch, "E208.orphan", {"position": v(-370.73, -255.55) * mm});
            skPoint(sketch, "E209.orphan", {"position": v(-373.57, -255.55) * mm});
            skPoint(sketch, "E210.orphan", {"position": v(-380.5, -252.7) * mm});
            skPoint(sketch, "E211.orphan", {"position": v(-383.33, -252.7) * mm});
            skPoint(sketch, "E212.orphan", {"position": v(-362.9, -254.48) * mm});
            skPoint(sketch, "E213.orphan", {"position": v(-357.93, -255.55) * mm});
            skPoint(sketch, "E214.orphan", {"position": v(-355.09, -255.55) * mm});
            skPoint(sketch, "E193.bottom.start.orphan", {"position": v(-348.17, -252.7) * mm});
            skPoint(sketch, "E215.orphan", {"position": v(-345.33, -252.7) * mm});
            skPoint(sketch, "E216.orphan", {"position": v(-365.76, -254.48) * mm});
            skArc(sketch, "E217.trimOffspring", {"start": v(-380.5, -245.37) * mm, "mid": v(-377.16, -247.4) * mm, "end": v(-373.57, -248.96) * mm});
            skArc(sketch, "E218", {"start": v(-373.57, -196.37) * mm, "mid": v(-377.47, -197.33) * mm, "end": v(-380.5, -199.96) * mm});
            skLineSegment(sketch, "E219.bottom", {"start": v(-242.86, -248.61) * mm, "end": v(-309.57, -248.61) * mm});
            skLineSegment(sketch, "E219.top", {"start": v(-242.86, -212.3) * mm, "end": v(-309.57, -212.3) * mm});
            skLineSegment(sketch, "E219.left", {"start": v(-242.86, -248.61) * mm, "end": v(-242.86, -212.3) * mm});
            skLineSegment(sketch, "E219.right", {"start": v(-309.57, -248.61) * mm, "end": v(-309.57, -212.3) * mm});
            skPoint(sketch, "E219.middle", {"position": v(-276.22, -230.46) * mm});
            skPoint(sketch, "E220.visualSharp", {"position": v(-208.6, 199) * mm});
            skArc(sketch, "E220.filletArc", {"start": v(-201.66, 199) * mm, "mid": v(-205.71, 196.92) * mm, "end": v(-206.4, 192.41) * mm});
            skPoint(sketch, "E221.visualSharp", {"position": v(-134.36, 199) * mm});
            skArc(sketch, "E221.filletArc", {"start": v(-133.22, 195.57) * mm, "mid": v(-135.04, 198.05) * mm, "end": v(-137.97, 199) * mm});
            skPoint(sketch, "E222.visualSharp", {"position": v(-6.11, -185.75) * mm});
            skArc(sketch, "E222.filletArc", {"start": v(-7.25, -182.33) * mm, "mid": v(-5.43, -184.8) * mm, "end": v(-2.51, -185.75) * mm});
            skLineSegment(sketch, "E223", {"start": v(45.83, -190.2) * mm, "end": v(45.83, -185.75) * mm});
            skLineSegment(sketch, "E224", {"start": v(18.43, -190.2) * mm, "end": v(18.43, -185.75) * mm});
            skLineSegment(sketch, "E225", {"start": v(18.43, -185.75) * mm, "end": v(17.92, -185.75) * mm});
            skLineSegment(sketch, "E226", {"start": v(-118.75, -230.86) * mm, "end": v(-125.08, -230.86) * mm});
            skLineSegment(sketch, "E227", {"start": v(-125.08, -230.86) * mm, "end": v(-125.08, -229.86) * mm});
            skPoint(sketch, "E228.middle", {"position": v(-69.63, -221.14) * mm});
            skPoint(sketch, "E228.middle.positionSnap0", {"position": v(-79.2, -221.14) * mm});
            skPoint(sketch, "E228.centerSnap0", {"position": v(-79.2, -221.14) * mm});
            skPoint(sketch, "E229.orphan", {"position": v(-79.2, -227.34) * mm});
            skPoint(sketch, "E230.MirrorCS.end.orphan", {"position": v(-74.72, -215.04) * mm});
            skPoint(sketch, "E230.MirrorCS.start.orphan", {"position": v(-79.2, -214.94) * mm});
            skLineSegment(sketch, "E231", {"start": v(-75.9, -230.97) * mm, "end": v(-75.9, -230.86) * mm});
            skLineSegment(sketch, "E232", {"start": v(-75.9, -215.57) * mm, "end": v(-75.9, -215.66) * mm});
            skLineSegment(sketch, "E233", {"start": v(-75.9, -247.5) * mm, "end": v(-75.9, -248.5) * mm});
            skLineSegment(sketch, "E234", {"start": v(-80.35, -247.5) * mm, "end": v(-80.35, -248.5) * mm});
            skLineSegment(sketch, "E235", {"start": v(175.66, -299.5) * mm, "end": v(172.76, -299.5) * mm});
            skLineSegment(sketch, "E236", {"start": v(172.76, -299.5) * mm, "end": v(172.76, -293.17) * mm});
            skLineSegment(sketch, "E237", {"start": v(197.46, -299.5) * mm, "end": v(197.46, -777.95) * mm});
            skPoint(sketch, "E238.MirrorCS.start.orphan", {"position": v(172.76, -266.77) * mm});
            skPoint(sketch, "E239.orphan", {"position": v(93.97, -266.77) * mm});
            skPoint(sketch, "E148.top.start.orphan", {"position": v(41.14, -260.44) * mm});
            skPoint(sketch, "E148.right.end.orphan", {"position": v(-41.14, -260.44) * mm});
            skLineSegment(sketch, "E240.bottom", {"start": v(-80.35, -266.77) * mm, "end": v(-40.94, -266.77) * mm});
            skLineSegment(sketch, "E241.top", {"start": v(93.97, -260.44) * mm, "end": v(172.76, -260.44) * mm});
            skLineSegment(sketch, "E241.left", {"start": v(93.97, -266.77) * mm, "end": v(93.97, -260.44) * mm});
            skLineSegment(sketch, "E242.trimOffspring", {"start": v(41.34, -266.77) * mm, "end": v(93.97, -266.77) * mm});
            skLineSegment(sketch, "E243.top", {"start": v(-40.94, -260.44) * mm, "end": v(41.34, -260.44) * mm});
            skLineSegment(sketch, "E243.left", {"start": v(-40.94, -266.77) * mm, "end": v(-40.94, -260.44) * mm});
            skLineSegment(sketch, "E243.right", {"start": v(41.34, -266.77) * mm, "end": v(41.34, -260.44) * mm});
            skLineSegment(sketch, "E244", {"start": v(199.34, -266.77) * mm, "end": v(172.76, -266.77) * mm});
            skLineSegment(sketch, "E245", {"start": v(172.76, -266.77) * mm, "end": v(172.76, -260.44) * mm});
            skLineSegment(sketch, "E246.left", {"start": v(-80.35, -185.59) * mm, "end": v(-80.35, -200.88) * mm});
            skLineSegment(sketch, "E247.MirrorCS", {"start": v(-74.02, -247.73) * mm, "end": v(-74.02, -231.2) * mm});
            skLineSegment(sketch, "E248.MirrorCS", {"start": v(-80.35, -200.88) * mm, "end": v(-74.02, -200.88) * mm});
            skLineSegment(sketch, "E249.trimOffspring", {"start": v(-80.35, -248.73) * mm, "end": v(-80.35, -267.01) * mm});
            skLineSegment(sketch, "E250", {"start": v(-80.35, -231.2) * mm, "end": v(-74.02, -231.2) * mm});
            skLineSegment(sketch, "E251", {"start": v(-74.02, -215.4) * mm, "end": v(-80.35, -215.4) * mm});
            skLineSegment(sketch, "E252", {"start": v(-80.35, -215.4) * mm, "end": v(-80.35, -231.2) * mm});
            skLineSegment(sketch, "E253", {"start": v(-74.02, -247.73) * mm, "end": v(-80.35, -247.73) * mm});
            skLineSegment(sketch, "E254", {"start": v(-80.35, -247.73) * mm, "end": v(-80.35, -248.73) * mm});
            skLineSegment(sketch, "E255", {"start": v(-74.02, -215.4) * mm, "end": v(-74.02, -200.88) * mm});
            skLineSegment(sketch, "E256", {"start": v(-80.35, -185.75) * mm, "end": v(-80.35, -184.23) * mm});
            skLineSegment(sketch, "E257", {"start": v(-80.35, -184.23) * mm, "end": v(-80.85, -184.23) * mm});
            skSolve(sketch);
        }
        {
            var Q0;
            Q0=makeQuery(id+"F0.imprint","IMPRINT",FACE,{"disambiguationData":[TD([[makeQuery(id+"F0.imprint","IMPRINT",EDGE,{"derivedFrom":sQuery(id+"F0.wireOp",EDGE,"E151.bottom")}),-1.0]])]});
            var Q1;
            Q1=makeQuery(id+"F0.imprint","IMPRINT",FACE,{"disambiguationData":[TD([[makeQuery(id+"F0.imprint","IMPRINT",EDGE,{"derivedFrom":sQuery(id+"F0.wireOp",EDGE,"E136.bottom")}),-1.0]])]});
            var Q2;
            {var subQ4=sQuery(id+"F0.wireOp",EDGE,"sC4kQ6F8-xUsw-eNn1-kUFQ-Rawnznmu5okk");Q2=makeQuery(id+"F0.imprint","IMPRINT",FACE,{"disambiguationData":[TD([[makeQuery(id+"F0.imprint","IMPRINT",EDGE,{"derivedFrom":subQ4}),-1.0]])]});}
            var Q3;
            Q3=makeQuery(id+"F0.imprint","IMPRINT",FACE,{"disambiguationData":[TD([[makeQuery(id+"F0.imprint","IMPRINT",EDGE,{"derivedFrom":sQuery(id+"F0.wireOp",EDGE,"E118.bottom")}),-1.0]])]});
            var Q4;
            Q4=makeQuery(id+"F0.imprint","IMPRINT",FACE,{"disambiguationData":[TD([[makeQuery(id+"F0.imprint","IMPRINT",EDGE,{"derivedFrom":sQuery(id+"F0.wireOp",EDGE,"E24.bottom")}),1.0]])]});
            var Q5;
            Q5=makeQuery(id+"F0.imprint","IMPRINT",FACE,{"disambiguationData":[TD([[makeQuery(id+"F0.imprint","IMPRINT",EDGE,{"derivedFrom":sQuery(id+"F0.wireOp",EDGE,"E53.MirrorCS")}),1.0]])]});
            var Q6;
            Q6=makeQuery(id+"F0.imprint","IMPRINT",FACE,{"disambiguationData":[TD([[makeQuery(id+"F0.imprint","IMPRINT",EDGE,{"derivedFrom":sQuery(id+"F0.wireOp",EDGE,"E48.MirrorCS")}),1.0]])]});
            var Q7;
            Q7=makeQuery(id+"F0.imprint","IMPRINT",FACE,{"disambiguationData":[TD([[makeQuery(id+"F0.imprint","IMPRINT",EDGE,{"derivedFrom":sQuery(id+"F0.wireOp",EDGE,"E70.MirrorCS")}),1.0]])]});
            var Q8;
            Q8=makeQuery(id+"F0.imprint","IMPRINT",FACE,{"disambiguationData":[TD([[makeQuery(id+"F0.imprint","IMPRINT",EDGE,{"derivedFrom":sQuery(id+"F0.wireOp",EDGE,"E86.MirrorCS")}),1.0]])]});
            var Q9;
            Q9=makeQuery(id+"F0.imprint","IMPRINT",FACE,{"disambiguationData":[TD([[makeQuery(id+"F0.imprint","IMPRINT",EDGE,{"derivedFrom":sQuery(id+"F0.wireOp",EDGE,"E0.0")}),-1.0]])]});
            extrude(context, id + "F1", {"entities" : qUnion([Q0, Q1, Q2, Q3, Q4, Q5, Q6, Q7, Q8, Q9]), "depth" : 4.45 * mm, "offsetDistance" : 25 * mm});
        }
    });
